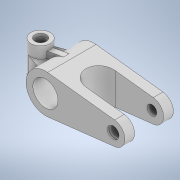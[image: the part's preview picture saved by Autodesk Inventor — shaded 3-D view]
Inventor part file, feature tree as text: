
AUTODESK INVENTOR PART (.ipt)
format: ipt  version: 2021 (Build 250183000, 183)  size: 198,144 bytes
history: native  units: mm
features: sketch x8, extrude x7, other x3, hole x1
ambient origin geometry x8: Origin, YZ Plane, XZ Plane, XY Plane, X Axis, Y Axis, Z Axis, Center Point
bodies: Body1 (feature_tree)
feature tree (19):
  other  "Sólido1"
  extrude  "Extrusão1"  Depth=100.0mm
  other  "Plano de trabalho1"
  extrude  "Extrusão2"  Depth=175.0mm
  extrude  "Extrusão3"  Depth=125.0mm TaperAngle=0.0deg
  other  "Plano de trabalho2"
  extrude  "Extrusão4"  Depth=50.0mm
  extrude  "Extrusão5"  Depth=80.0mm TaperAngle=0.0deg
  hole  "Furo1"  [1 undecoded]
  extrude  "Extrusão6"  Depth=100.0mm
  extrude  "Extrusão7"  Depth=15.0mm TaperAngle=0.0deg
  sketch  "Esboço1"  dims[d0=100.0mm d1=60.0mm]
  sketch  "Esboço2"  dims[d2=175.0mm d3=65.0mm]
  sketch  "Esboço3"  dims[d4=25.0mm d5=125.0mm d6=0.0mm]
  sketch  "Esboço4"  dims[d7=-25.0mm d8=50.0mm]
  sketch  "Esboço5"  dims[d9=75.0mm d10=80.0mm d11=0.0mm]
  sketch  "Esboço6"  dims[d12=3.490659mm d13=50.0mm d14=0.0mm]
  sketch  "Esboço7"  dims[d15=62.5mm d16=100.0mm]
  sketch  "Esboço8"  dims[d17=13.962634mm d18=15.0mm d19=0.0mm d20=75.0mm d21=80.0mm d22=0.0mm d23=0.0mm d24=25.0mm d25=6.0mm d26=30.0mm d27=8.0mm d28=90.0deg d29=8.0mm d30=20.594885mm d31=30.0mm d32=2.5mm d33=0.0mm d34=30.0mm d35=2.5mm d36=0.0mm]
note: 1 required parameter value undecoded (feature->parameter linkage not recoverable at this tier; creation-order binding heuristic only, values carry confidence <= 0.55)
